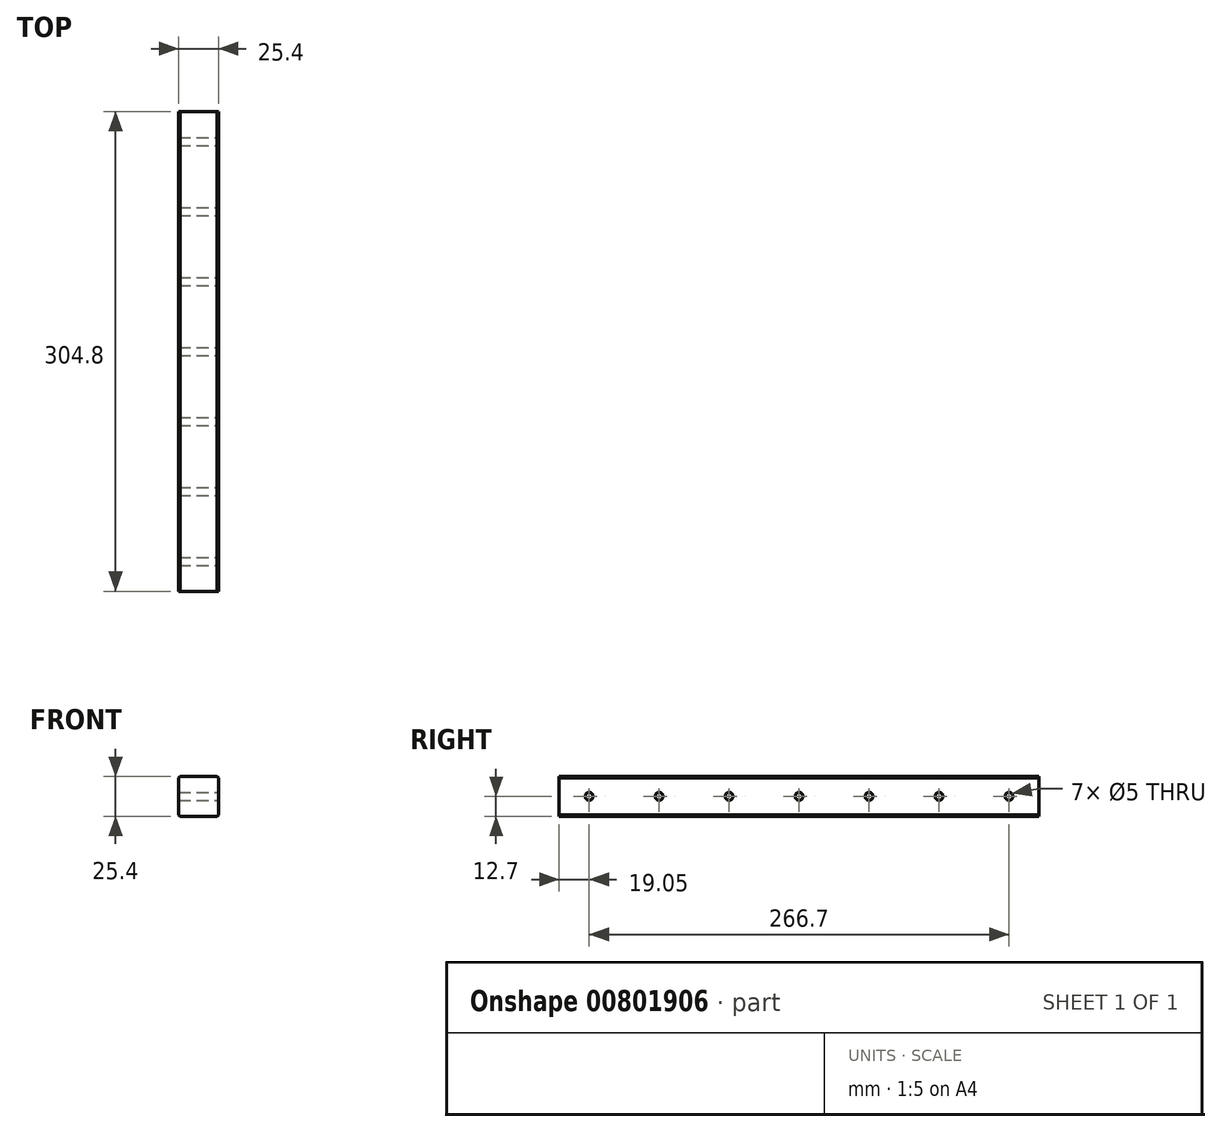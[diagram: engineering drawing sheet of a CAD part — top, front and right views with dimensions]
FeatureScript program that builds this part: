
annotation { "Feature Type Name" : "Feature", "Feature Type Description" : "" }
export const myFeature = defineFeature(function(context is Context, id is Id, definition is map)
    precondition{}
    {
        {
            var Q0;
            Q0=qCreatedBy(makeId("Front.planeOp"),FACE);
            var sketch = newSketch(context, id + "F0", { "sketchPlane" : qUnion([Q0])});
            skLineSegment(sketch, "E0.bottom", {"start": v(12.7, -12.7) * mm, "end": v(-12.7, -12.7) * mm});
            skLineSegment(sketch, "E0.top", {"start": v(12.7, 12.7) * mm, "end": v(-12.7, 12.7) * mm});
            skLineSegment(sketch, "E0.left", {"start": v(12.7, -12.7) * mm, "end": v(12.7, 12.7) * mm});
            skLineSegment(sketch, "E0.right", {"start": v(-12.7, -12.7) * mm, "end": v(-12.7, 12.7) * mm});
            skPoint(sketch, "E0.middle", {"position": v(0, 0) * mm});
            skSolve(sketch);
        }
        {
            var Q0;
            Q0=qSketchRegion(id+"F0",true);
            extrude(context, id + "F1", {"entities" : qUnion([Q0]), "depth" : 304.8 * mm, "offsetDistance" : 25 * mm});
        }
        {
            var Q0;
            Q0=makeQuery(id+"F1.opExtrude","SWEPT_EDGE",EDGE,{"disambiguationData":[OSD([sQuery(id+"F0.wireOp",EDGE,"E0.top"),sQuery(id+"F0.wireOp",EDGE,"E0.left")])]});
            var Q1;
            Q1=makeQuery(id+"F1.opExtrude","SWEPT_EDGE",EDGE,{"disambiguationData":[OSD([sQuery(id+"F0.wireOp",EDGE,"E0.bottom"),sQuery(id+"F0.wireOp",EDGE,"E0.left")])]});
            var Q2;
            Q2=makeQuery(id+"F1.opExtrude","SWEPT_EDGE",EDGE,{"disambiguationData":[OSD([sQuery(id+"F0.wireOp",EDGE,"E0.top"),sQuery(id+"F0.wireOp",EDGE,"E0.right")])]});
            var Q3;
            Q3=makeQuery(id+"F1.opExtrude","SWEPT_EDGE",EDGE,{"disambiguationData":[OSD([sQuery(id+"F0.wireOp",EDGE,"E0.bottom"),sQuery(id+"F0.wireOp",EDGE,"E0.right")])]});
            chamfer(context, id + "F2", {"entities" : qUnion([Q0, Q1, Q2, Q3]), "width" : 1 * mm, "tangentPropagation" : true});
        }
        {
            var Q0;
            Q0=makeQuery(id+"F1.opExtrude","SWEPT_FACE",FACE,{"disambiguationData":[OSD([sQuery(id+"F0.wireOp",EDGE,"E0.left")])]});
            var sketch = newSketch(context, id + "F3", { "sketchPlane" : qUnion([Q0])});
            skPoint(sketch, "E1", {"position": v(-152.4, 0) * mm});
            skPoint(sketch, "E1.positionSnap0", {"position": v(-152.4, 11.7) * mm});
            skPoint(sketch, "E1.positionSnap1", {"position": v(-304.8, 0) * mm});
            skPoint(sketch, "E2.1.0.0", {"position": v(-107.95, 0) * mm});
            skPoint(sketch, "E2.2.0.0", {"position": v(-63.5, 0) * mm});
            skPoint(sketch, "E2.3.0.0", {"position": v(-19.05, 0) * mm});
            skLineSegment(sketch, "E2.direction1", {"start": v(-152.4, 0) * mm, "end": v(-107.95, 0) * mm, "construction": true});
            skPoint(sketch, "E3.1.0.0", {"position": v(-196.85, 0) * mm});
            skPoint(sketch, "E3.2.0.0", {"position": v(-241.3, 0) * mm});
            skPoint(sketch, "E3.3.0.0", {"position": v(-285.75, 0) * mm});
            skLineSegment(sketch, "E3.direction1", {"start": v(-152.4, 0) * mm, "end": v(-196.85, 0) * mm, "construction": true});
            skSolve(sketch);
        }
        {
            var Q0;
            Q0=sQuery(id+"F3.wireOp",VERTEX,"E3.3.0.0");
            var Q1;
            Q1=sQuery(id+"F3.wireOp",VERTEX,"E3.2.0.0");
            var Q2;
            Q2=sQuery(id+"F3.wireOp",VERTEX,"E3.1.0.0");
            var Q3;
            Q3=sQuery(id+"F3.wireOp",VERTEX,"E1");
            var Q4;
            Q4=sQuery(id+"F3.wireOp",VERTEX,"E2.1.0.0");
            var Q5;
            Q5=sQuery(id+"F3.wireOp",VERTEX,"E2.2.0.0");
            var Q6;
            Q6=sQuery(id+"F3.wireOp",VERTEX,"E2.3.0.0");
            var Q7;
            Q7=makeQuery(id+"F1.opExtrude","SWEPT_BODY",BODY,{"disambiguationData":[OSD([sQuery(id+"F0.wireOp",EDGE,"E0.bottom"),sQuery(id+"F0.wireOp",EDGE,"E0.top"),sQuery(id+"F0.wireOp",EDGE,"E0.left"),sQuery(id+"F0.wireOp",EDGE,"E0.right")])]});
            hole(context, id + "F4", {"style" : HoleStyle.SIMPLE, "endStyle" : HoleEndStyle.THROUGH, "standardTappedOrClearance" : lookupTablePath({ "standard" : "ISO", "engagement" : "75%", "pitch" : "1 mm", "size" : "M6", "type" : "Tapped" }), "standardBlindInLast" : lookupTablePath({ "standard" : "ISO", "fit" : "Normal", "engagement" : "75%", "pitch" : "1 mm", "size" : "M6", "type" : "Clearance & tapped" }), "holeDiameter" : 5 * mm, "majorDiameter" : 6 * mm, "showTappedDepth" : true, "isTappedThrough" : true, "tappedDepth" : 19.05 * mm, "tapClearance" : 3, "startFromSketch" : true, "locations" : qUnion([Q0, Q1, Q2, Q3, Q4, Q5, Q6]), "scope" : qUnion([Q7])});
        }
    });
